# Revit family: 7942, 7987 Mashiko 300 Square
name_source: partatom
category: Lighting Fixtures
revit_build: Autodesk Revit 2018 (Build: 20170223_1515(x64)
units: mm (PartAtom-declared; Revit-internal decimal feet)

## family parameters
Always vertical = Yes
Cut with Voids When Loaded = No
Host = Ceiling
Light Source = Yes
OmniClass Number = 23.80.70.11
OmniClass Title = Luminaries for Internal Lighting
Part Type = Normal
Room Calculation Point = No
Round Connector Dimension = Use Diameter
Shared = No

## types (2) — shared parameters
Color Filter = 16777215
Dimming Lamp Color Temperature Shift = <None>

## per-type parameters (varying)
| type | Apparent Load | Dimmable | Driver Included | Driver Required | Efficacy (lm/w) | Electrical Class | Lamp | Light Source Fixed | Location Rating | Main Material | Photometric Web File | Power (Watts) | Product Code | Product Location | Product Name | Product SKU | Tilt Angle |
| CE | 27 VA | No | Integral Driver | No | 62 | Class II | Dedicated LED | Yes | IP44 | Stainless Steel | TRN-18318.ies | 15.9 | 7942 | Bathroom / Indoor | Mashiko 300 Square LED | 1121040 | 0.00° |
| ETL | 0 VA |  |  |  |  |  |  |  |  |  | generic |  |  |  |  |  | 60.00° |

## geometry (parser evidence)
native form markers: Sweep x1
no freeform markers — native parametric forms only
